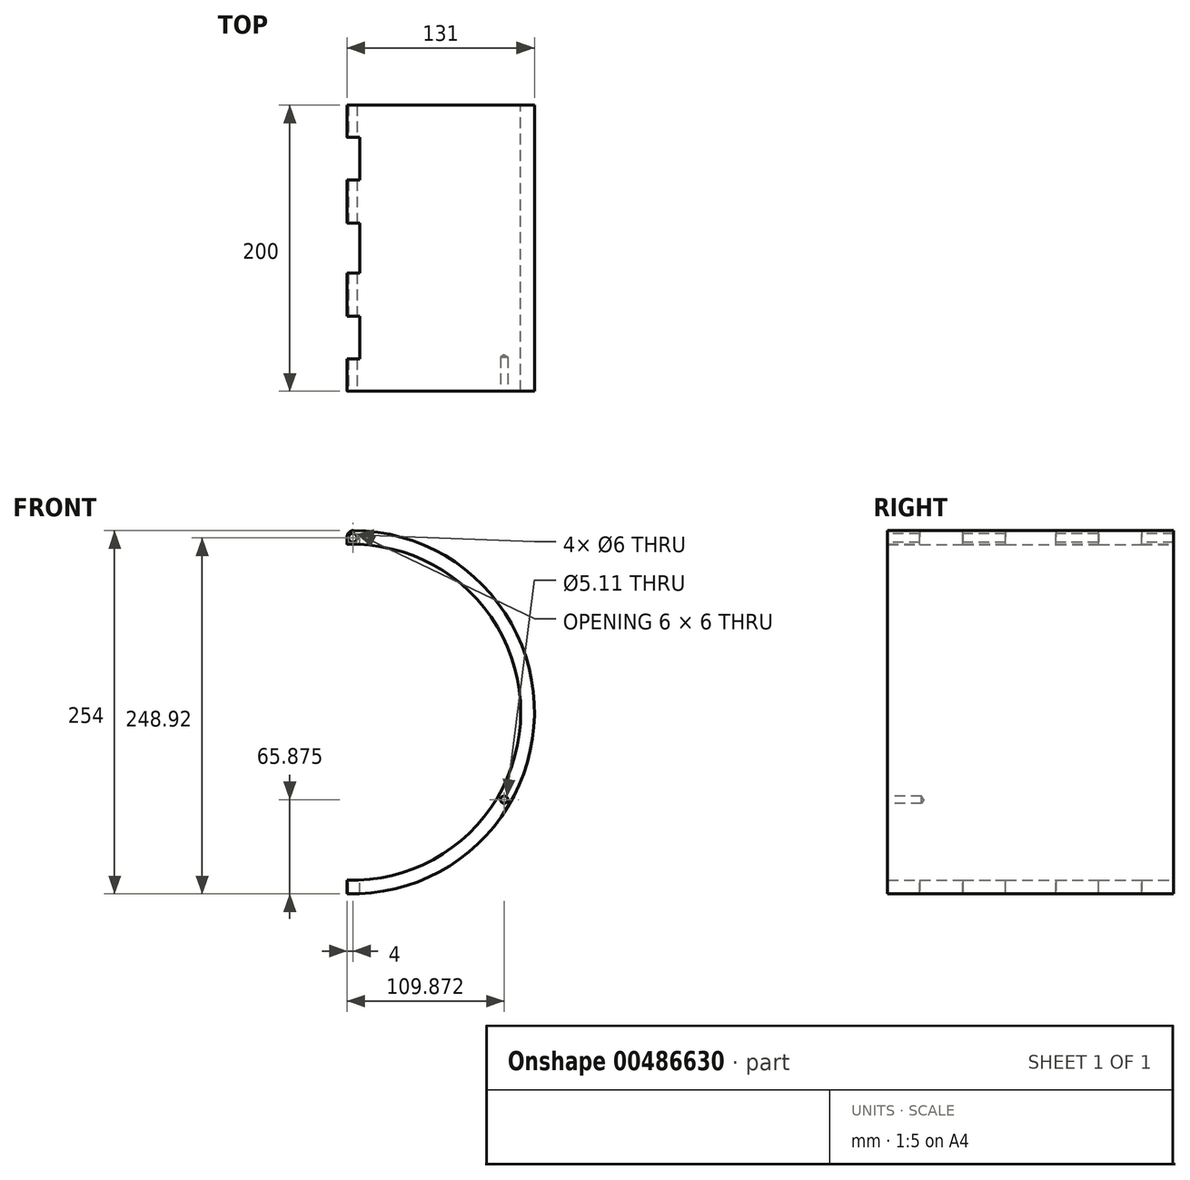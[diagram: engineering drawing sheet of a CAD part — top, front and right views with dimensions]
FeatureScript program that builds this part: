
annotation { "Feature Type Name" : "Feature", "Feature Type Description" : "" }
export const myFeature = defineFeature(function(context is Context, id is Id, definition is map)
    precondition{}
    {
        {
            var Q0;
            Q0=qCreatedBy(makeId("Front.planeOp"),FACE);
            var sketch = newSketch(context, id + "F0", { "sketchPlane" : qUnion([Q0])});
            skCircle(sketch, "E0", {"center": v(0, 0) * mm, "radius": 117.42 * mm});
            skCircle(sketch, "E1", {"center": v(0, 0) * mm, "radius": 127 * mm});
            skSolve(sketch);
        }
        {
            var Q0;
            Q0=makeQuery(id+"F0.imprint","IMPRINT",FACE,{"disambiguationData":[TD([[makeQuery(id+"F0.imprint","IMPRINT",EDGE,{"derivedFrom":sQuery(id+"F0.wireOp",EDGE,"E0")}),-1.0]])]});
            extrude(context, id + "F1", {"entities" : qUnion([Q0]), "endBound" : BoundingType.SYMMETRIC, "depth" : 200 * mm});
        }
        {
            var Q0;
            Q0=makeQuery(id+"F1.opExtrude","CAP_FACE",FACE,{"disambiguationData":[OSD([sQuery(id+"F0.wireOp",EDGE,"E0"),sQuery(id+"F0.wireOp",EDGE,"E1")])],"isStart":false});
            var sketch = newSketch(context, id + "F2", { "sketchPlane" : qUnion([Q0])});
            skCircle(sketch, "E2", {"center": v(0, 121.92) * mm, "radius": 3 * mm});
            skSolve(sketch);
        }
        {
            var Q0;
            Q0=makeQuery(id+"F2.imprint","IMPRINT",FACE,{"disambiguationData":[TD([[makeQuery(id+"F2.imprint","IMPRINT",EDGE,{"derivedFrom":sQuery(id+"F2.wireOp",EDGE,"E2")}),1.0]])]});
            extrude(context, id + "F3", {"entities" : qUnion([Q0]), "operationType" : NewBodyOperationType.REMOVE, "endBound" : BoundingType.THROUGH_ALL, "oppositeDirection" : true, "depth" : 25 * mm});
        }
        {
            var Q0;
            Q0=qCreatedBy(makeId("Top.planeOp"),FACE);
            var sketch = newSketch(context, id + "F4", { "sketchPlane" : qUnion([Q0])});
            skLineSegment(sketch, "E3", {"start": v(0, 100.89) * mm, "end": v(0, -112.88) * mm, "construction": true});
            skLineSegment(sketch, "E4", {"start": v(-85.43, 0) * mm, "end": v(71.36, 0) * mm, "construction": true});
            skLineSegment(sketch, "E5", {"start": v(-4, 104.48) * mm, "end": v(-4, 77.5) * mm});
            skLineSegment(sketch, "E6", {"start": v(5, 47.5) * mm, "end": v(-4, 47.5) * mm});
            skLineSegment(sketch, "E7", {"start": v(-4, 47.5) * mm, "end": v(-4, 17.5) * mm});
            skLineSegment(sketch, "E8", {"start": v(-4, 17.5) * mm, "end": v(5, 17.5) * mm});
            skLineSegment(sketch, "E9.0", {"start": v(5, 77.5) * mm, "end": v(5, 47.5) * mm});
            skLineSegment(sketch, "E10.MirrorCS", {"start": v(5, -47.5) * mm, "end": v(-4, -47.5) * mm});
            skLineSegment(sketch, "E11.MirrorCS", {"start": v(-4, -104.48) * mm, "end": v(-4, -77.5) * mm});
            skLineSegment(sketch, "E12.MirrorCS", {"start": v(-4, -77.5) * mm, "end": v(5, -77.5) * mm});
            skLineSegment(sketch, "E13.MirrorCS", {"start": v(5, -77.5) * mm, "end": v(5, -47.5) * mm});
            skLineSegment(sketch, "E14.MirrorCS", {"start": v(-4, -47.5) * mm, "end": v(-4, -17.5) * mm});
            skLineSegment(sketch, "E15.MirrorCS", {"start": v(-4, -17.5) * mm, "end": v(5, -17.5) * mm});
            skLineSegment(sketch, "E16", {"start": v(-5, 104.48) * mm, "end": v(-4, 104.48) * mm});
            skLineSegment(sketch, "E17", {"start": v(-5, -104.48) * mm, "end": v(-4, -104.48) * mm});
            skLineSegment(sketch, "E18", {"start": v(-4, 77.5) * mm, "end": v(5, 77.5) * mm});
            skLineSegment(sketch, "E19", {"start": v(5, -17.5) * mm, "end": v(5, 17.5) * mm});
            skLineSegment(sketch, "E20", {"start": v(-5, 104.48) * mm, "end": v(-141.1, 104.48) * mm});
            skLineSegment(sketch, "E21", {"start": v(-141.1, 104.48) * mm, "end": v(-141.1, -104.48) * mm});
            skLineSegment(sketch, "E22", {"start": v(-141.1, -104.48) * mm, "end": v(-5, -104.48) * mm});
            skSolve(sketch);
        }
        {
            var Q0;
            Q0=makeQuery(id+"F4.imprint","IMPRINT",FACE,{"disambiguationData":[TD([[makeQuery(id+"F4.imprint","IMPRINT",EDGE,{"derivedFrom":sQuery(id+"F4.wireOp",EDGE,"E5")}),-1.0]])]});
            extrude(context, id + "F5", {"entities" : qUnion([Q0]), "operationType" : NewBodyOperationType.REMOVE, "endBound" : BoundingType.SYMMETRIC, "oppositeDirection" : true, "depth" : 300 * mm});
        }
        {
            var Q0;
            Q0=makeQuery(id+"F5.boolean.opBoolean","INTERSECT",EDGE,{"disambiguationData":[OD(1.0)],"derivedFrom":[makeQuery(id+"F1.opExtrude","SWEPT_FACE",FACE,{"disambiguationData":[OSD([sQuery(id+"F0.wireOp",EDGE,"E1")])]}),makeQuery(id+"F5.opExtrude","SWEPT_FACE",FACE,{"disambiguationData":[OSD([sQuery(id+"F4.wireOp",EDGE,"E11.MirrorCS")])]})]});
            var Q1;
            Q1=makeQuery(id+"F5.boolean.opBoolean","INTERSECT",EDGE,{"disambiguationData":[OD(1.0)],"derivedFrom":[makeQuery(id+"F1.opExtrude","SWEPT_FACE",FACE,{"disambiguationData":[OSD([sQuery(id+"F0.wireOp",EDGE,"E1")])]}),makeQuery(id+"F5.opExtrude","SWEPT_FACE",FACE,{"disambiguationData":[OSD([sQuery(id+"F4.wireOp",EDGE,"E14.MirrorCS")])]})]});
            var Q2;
            Q2=makeQuery(id+"F5.boolean.opBoolean","INTERSECT",EDGE,{"disambiguationData":[OD(1.0)],"derivedFrom":[makeQuery(id+"F1.opExtrude","SWEPT_FACE",FACE,{"disambiguationData":[OSD([sQuery(id+"F0.wireOp",EDGE,"E1")])]}),makeQuery(id+"F5.opExtrude","SWEPT_FACE",FACE,{"disambiguationData":[OSD([sQuery(id+"F4.wireOp",EDGE,"E7")])]})]});
            var Q3;
            Q3=makeQuery(id+"F5.boolean.opBoolean","INTERSECT",EDGE,{"disambiguationData":[OD(1.0)],"derivedFrom":[makeQuery(id+"F1.opExtrude","SWEPT_FACE",FACE,{"disambiguationData":[OSD([sQuery(id+"F0.wireOp",EDGE,"E1")])]}),makeQuery(id+"F5.opExtrude","SWEPT_FACE",FACE,{"disambiguationData":[OSD([sQuery(id+"F4.wireOp",EDGE,"E5")])]})]});
            fillet(context, id + "F6", {"entities" : qUnion([Q0, Q1, Q2, Q3]), "radius" : 4.5 * mm, "tangentPropagation" : true, "allowEdgeOverflow" : false});
        }
        {
            var Q0;
            Q0=makeQuery(id+"F5.boolean.opBoolean","COPY",EDGE,{"disambiguationData":[OD(0.0)],"derivedFrom":makeQuery(id+"F5.opExtrude","SWEPT_EDGE",EDGE,{"disambiguationData":[OSD([sQuery(id+"F4.wireOp",EDGE,"E7"),sQuery(id+"F4.wireOp",EDGE,"E8")])]})});
            var Q1;
            Q1=makeQuery(id+"F5.boolean.opBoolean","COPY",EDGE,{"disambiguationData":[OD(0.0)],"derivedFrom":makeQuery(id+"F5.opExtrude","SWEPT_EDGE",EDGE,{"disambiguationData":[OSD([sQuery(id+"F4.wireOp",EDGE,"E10.MirrorCS"),sQuery(id+"F4.wireOp",EDGE,"E14.MirrorCS")])]})});
            var Q2;
            Q2=makeQuery(id+"F5.boolean.opBoolean","COPY",EDGE,{"disambiguationData":[OD(0.0)],"derivedFrom":makeQuery(id+"F5.opExtrude","SWEPT_EDGE",EDGE,{"disambiguationData":[OSD([sQuery(id+"F4.wireOp",EDGE,"E5"),sQuery(id+"F4.wireOp",EDGE,"E18")])]})});
            chamfer(context, id + "F7", {"entities" : qUnion([Q0, Q1, Q2]), "chamferType" : ChamferType.OFFSET_ANGLE, "width" : 1 * mm, "oppositeDirection" : true, "angle" : 15 * degree, "tangentPropagation" : true});
        }
        {
            var Q0;
            Q0=makeQuery(id+"F5.boolean.opBoolean","COPY",EDGE,{"disambiguationData":[OD(0.0)],"derivedFrom":makeQuery(id+"F5.opExtrude","SWEPT_EDGE",EDGE,{"disambiguationData":[OSD([sQuery(id+"F4.wireOp",EDGE,"E6"),sQuery(id+"F4.wireOp",EDGE,"E7")])]})});
            var Q1;
            Q1=makeQuery(id+"F5.boolean.opBoolean","COPY",EDGE,{"disambiguationData":[OD(0.0)],"derivedFrom":makeQuery(id+"F5.opExtrude","SWEPT_EDGE",EDGE,{"disambiguationData":[OSD([sQuery(id+"F4.wireOp",EDGE,"E14.MirrorCS"),sQuery(id+"F4.wireOp",EDGE,"E15.MirrorCS")])]})});
            var Q2;
            Q2=makeQuery(id+"F5.boolean.opBoolean","COPY",EDGE,{"disambiguationData":[OD(0.0)],"derivedFrom":makeQuery(id+"F5.opExtrude","SWEPT_EDGE",EDGE,{"disambiguationData":[OSD([sQuery(id+"F4.wireOp",EDGE,"E11.MirrorCS"),sQuery(id+"F4.wireOp",EDGE,"E12.MirrorCS")])]})});
            chamfer(context, id + "F8", {"entities" : qUnion([Q0, Q1, Q2]), "chamferType" : ChamferType.OFFSET_ANGLE, "width" : 1 * mm, "oppositeDirection" : false, "angle" : 15 * degree, "tangentPropagation" : true});
        }
        {
            var Q0;
            Q0=makeQuery(id+"F1.opExtrude","CAP_FACE",FACE,{"disambiguationData":[OSD([sQuery(id+"F0.wireOp",EDGE,"E0"),sQuery(id+"F0.wireOp",EDGE,"E1")])],"isStart":false});
            var sketch = newSketch(context, id + "F9", { "sketchPlane" : qUnion([Q0])});
            skCircle(sketch, "E23", {"center": v(0, 0) * mm, "radius": 122.25 * mm, "construction": true});
            skLineSegment(sketch, "E24", {"start": v(132.09, -73.89) * mm, "end": v(122.71, -70.85) * mm, "construction": true});
            skLineSegment(sketch, "E25", {"start": v(122.71, -70.85) * mm, "end": v(0, 0) * mm, "construction": true});
            skLineSegment(sketch, "E26", {"start": v(0, 0) * mm, "end": v(161.65, 0) * mm, "construction": true});
            skPoint(sketch, "E27", {"position": v(105.87, -61.12) * mm});
            skSolve(sketch);
        }
        {
            var Q0;
            Q0=sQuery(id+"F9.wireOp",VERTEX,"E27");
            var Q1;
            Q1=makeQuery(id+"F1.opExtrude","SWEPT_BODY",BODY,{"disambiguationData":[OSD([sQuery(id+"F0.wireOp",EDGE,"E0"),sQuery(id+"F0.wireOp",EDGE,"E1")])]});
            hole(context, id + "F10", {"style" : HoleStyle.SIMPLE, "endStyle" : HoleEndStyle.BLIND, "standardTappedOrClearance" : lookupTablePath({ "standard" : "ANSI", "engagement" : "75%", "pitch" : "20 tpi", "size" : "1/4", "type" : "Tapped" }), "standardBlindInLast" : lookupTablePath({ "standard" : "ANSI", "engagement" : "75%", "pitch" : "20 tpi", "size" : "1/4", "type" : "Tapped" }), "holeDiameter" : 5.1 * mm, "showTappedDepth" : true, "holeDepth" : 23.8 * mm, "isTappedThrough" : true, "tappedDepth" : 20 * mm, "tapClearance" : 3, "startFromSketch" : true, "locations" : qUnion([Q0]), "scope" : qUnion([Q1]), "majorDiameter" : 6.35 * mm});
        }
    });
